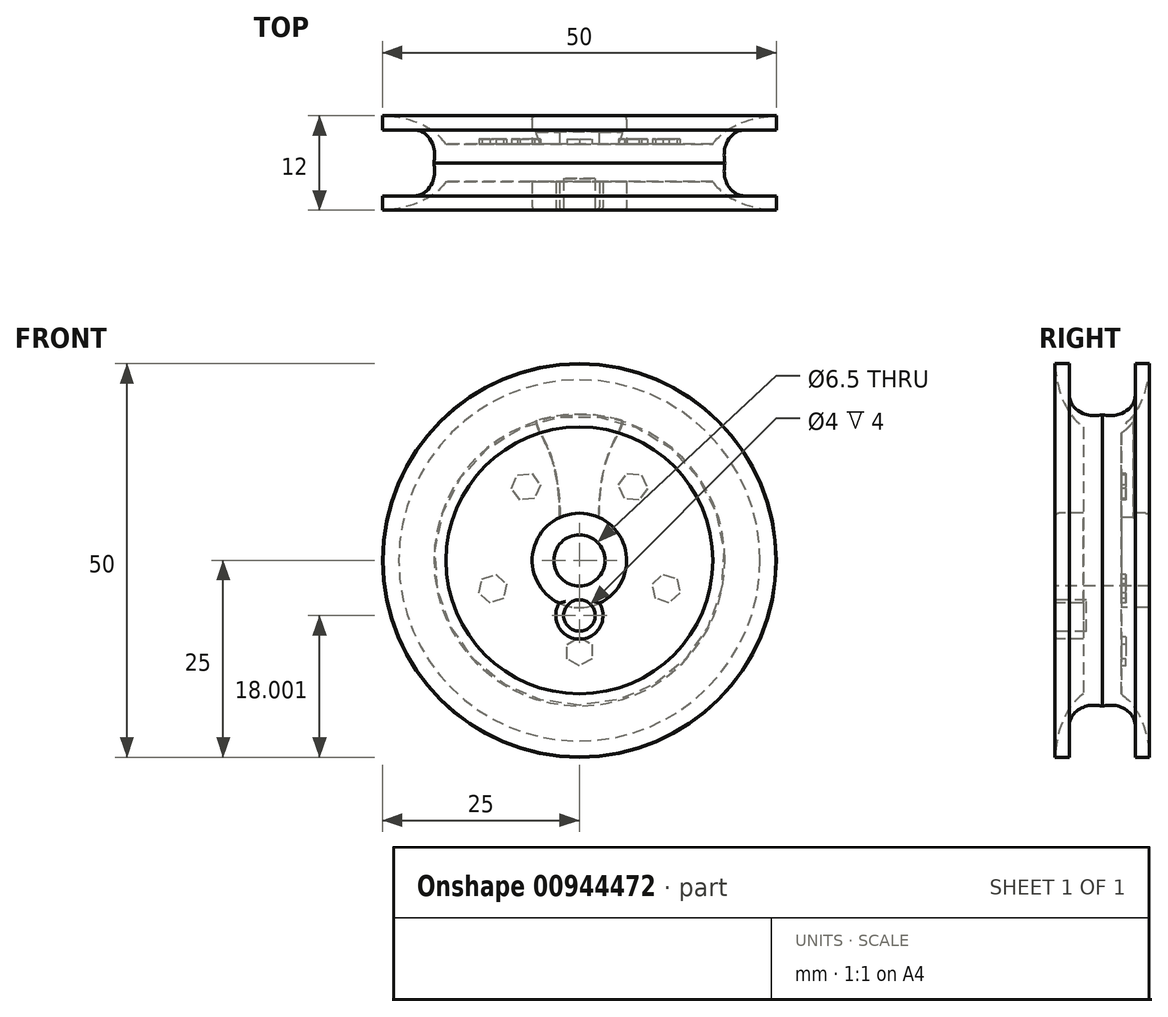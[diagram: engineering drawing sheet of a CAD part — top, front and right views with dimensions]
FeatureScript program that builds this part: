
annotation { "Feature Type Name" : "Feature", "Feature Type Description" : "" }
export const myFeature = defineFeature(function(context is Context, id is Id, definition is map)
    precondition{}
    {
        {
            var Q0;
            Q0=qCreatedBy(makeId("Front.planeOp"),FACE);
            var sketch = newSketch(context, id + "F0", { "sketchPlane" : qUnion([Q0])});
            skCircle(sketch, "E0", {"center": v(0, 0) * mm, "radius": 25 * mm});
            skSolve(sketch);
        }
        {
            var Q0;
            Q0 = qSketchRegion(id + "F0", true);
            extrude(context, id + "F1", {"entities" : qUnion([Q0]), "depth" : 12 * mm, "offsetDistance" : 25 * mm});
        }
        {
            var Q0;
            Q0=makeQuery(id+"F1.opExtrude","CAP_FACE",FACE,{"disambiguationData":[OSD([sQuery(id+"F0.wireOp",EDGE,"E0")])],"isStart":false});
            var sketch = newSketch(context, id + "F2", { "sketchPlane" : qUnion([Q0])});
            skSolve(sketch);
        }
        {
            var Q0;
            Q0=makeQuery(id+"F2.imprint","IMPRINT",FACE,{"disambiguationData":[TD([[makeQuery(id+"F2.imprint","IMPRINT",EDGE,{"derivedFrom":makeQuery(id+"F1.opExtrude","CAP_EDGE",EDGE,{"disambiguationData":[OSD([sQuery(id+"F0.wireOp",EDGE,"E0")])],"isStart":false})}),1.0]])]});
            var sketch = newSketch(context, id + "F3", { "sketchPlane" : qUnion([Q0])});
            skCircle(sketch, "E1", {"center": v(0, 0) * mm, "radius": 3.25 * mm});
            skSolve(sketch);
        }
        {
            var Q0;
            Q0 = qSketchRegion(id + "F3", true);
            extrude(context, id + "F4", {"entities" : qUnion([Q0]), "operationType" : NewBodyOperationType.REMOVE, "endBound" : BoundingType.THROUGH_ALL, "oppositeDirection" : true, "depth" : 25 * mm, "offsetDistance" : 25 * mm});
        }
        {
            var Q0;
            Q0=qCreatedBy(makeId("Top.planeOp"),FACE);
            var sketch = newSketch(context, id + "F5", { "sketchPlane" : qUnion([Q0])});
            skLineSegment(sketch, "E2", {"start": v(-24.95, 0) * mm, "end": v(-24.95, -3.6) * mm, "construction": true});
            skLineSegment(sketch, "E3", {"start": v(-24.95, -3.6) * mm, "end": v(-16.95, -3.6) * mm, "construction": true});
            skFitSpline(sketch, "E4", {"points": [v(-24.95, 0) * mm, v(-16.95, -3.6) * mm], "startDerivative": vector(8.9, -0.49) * mm, "endDerivative": vector(5.24, -7.32) * mm});
            skLineSegment(sketch, "E5", {"start": v(0, 0) * mm, "end": v(0, -6) * mm, "construction": true});
            skLineSegment(sketch, "E6", {"start": v(0, -6) * mm, "end": v(-25.37, -6) * mm, "construction": true});
            skLineSegment(sketch, "E7", {"start": v(0, 0) * mm, "end": v(-24.95, 0) * mm});
            skLineSegment(sketch, "E8", {"start": v(-16.95, -3.6) * mm, "end": v(0, -3.6) * mm});
            skLineSegment(sketch, "E9", {"start": v(0, -3.6) * mm, "end": v(0, 0) * mm});
            skLineSegment(sketch, "E10.MirrorCS", {"start": v(-16.95, -8.4) * mm, "end": v(0, -8.4) * mm});
            skFitSpline(sketch, "E11.MirrorCS", {"points": [v(-24.95, -12) * mm, v(-16.95, -8.4) * mm], "startDerivative": vector(8.9, 0.49) * mm, "endDerivative": vector(5.24, 7.32) * mm});
            skLineSegment(sketch, "E12.MirrorCS", {"start": v(0, -12) * mm, "end": v(-24.95, -12) * mm});
            skLineSegment(sketch, "E13.MirrorCS", {"start": v(0, -12) * mm, "end": v(0, -6) * mm, "construction": true});
            skLineSegment(sketch, "E14", {"start": v(0, -8.4) * mm, "end": v(0, -12) * mm});
            skLineSegment(sketch, "E15", {"start": v(-24.95, 0) * mm, "end": v(-24.95, -1.8) * mm, "construction": true});
            skLineSegment(sketch, "E16", {"start": v(-24.95, -1.8) * mm, "end": v(-22.95, -1.8) * mm, "construction": true});
            skLineSegment(sketch, "E17", {"start": v(-24.98, -6) * mm, "end": v(-18.48, -6) * mm});
            skFitSpline(sketch, "E18", {"points": [v(-22.95, -1.8) * mm, v(-18.48, -6) * mm], "startDerivative": vector(9.17, -0.94) * mm, "endDerivative": vector(0.05, -5.85) * mm});
            skLineSegment(sketch, "E19", {"start": v(-24.95, -1.8) * mm, "end": v(-26.85, -1.8) * mm});
            skLineSegment(sketch, "E20", {"start": v(-26.85, -1.8) * mm, "end": v(-25.37, -6) * mm});
            skLineSegment(sketch, "E21.MirrorCS", {"start": v(-26.85, -10.2) * mm, "end": v(-25.37, -6) * mm});
            skLineSegment(sketch, "E22.MirrorCS", {"start": v(-24.95, -10.2) * mm, "end": v(-26.85, -10.2) * mm});
            skLineSegment(sketch, "E23.MirrorCS", {"start": v(-24.95, -10.2) * mm, "end": v(-22.95, -10.2) * mm});
            skFitSpline(sketch, "E24.MirrorCS", {"points": [v(-22.95, -10.2) * mm, v(-18.48, -6) * mm], "startDerivative": vector(9.17, 0.94) * mm, "endDerivative": vector(0.05, 5.85) * mm});
            skLineSegment(sketch, "E25.MirrorCS", {"start": v(-24.95, -1.8) * mm, "end": v(-22.95, -1.8) * mm});
            skSolve(sketch);
        }
        {
            var Q0;
            Q0 = qSketchRegion(id + "F5", true);
            var Q1;
            Q1=sQuery(id+"F5.wireOp",EDGE,"E9");
            revolve(context, id + "F6", {"operationType" : NewBodyOperationType.REMOVE, "surfaceOperationType" : NewSurfaceOperationType.NEW, "entities" : qUnion([Q0]), "axis" : qUnion([Q1]), "revolveType" : RevolveType.FULL, "oppositeDirection" : true});
        }
        {
            var Q0;
            Q0=makeQuery(id+"F2.imprint","IMPRINT",FACE,{"disambiguationData":[TD([[makeQuery(id+"F2.imprint","IMPRINT",EDGE,{"derivedFrom":makeQuery(id+"F1.opExtrude","CAP_EDGE",EDGE,{"disambiguationData":[OSD([sQuery(id+"F0.wireOp",EDGE,"E0")])],"isStart":false})}),1.0]])]});
            var sketch = newSketch(context, id + "F7", { "sketchPlane" : qUnion([Q0])});
            skCircle(sketch, "E26", {"center": v(0, 0) * mm, "radius": 6 * mm});
            skCircle(sketch, "E27.0", {"center": v(0, 0) * mm, "radius": 3.25 * mm});
            skSolve(sketch);
        }
        {
            var Q0;
            Q0 = qSketchRegion(id + "F7", true);
            extrude(context, id + "F8", {"entities" : qUnion([Q0]), "operationType" : NewBodyOperationType.ADD, "oppositeDirection" : true, "depth" : 12 * mm, "offsetDistance" : 25 * mm});
        }
        {
            var Q0;
            Q0=qCreatedBy(makeId("Front.planeOp"),FACE);
            cPlane(context, id + "F9", {"entities" : qUnion([Q0]), "cplaneType" : CPlaneType.OFFSET, "offset" : 4 * mm, "width" : 150 * mm, "height" : 150 * mm});
        }
        {
            var Q0;
            Q0=qCreatedBy(id+"F9.planeOp",FACE);
            var sketch = newSketch(context, id + "F10", { "sketchPlane" : qUnion([Q0])});
            skLineSegment(sketch, "E28", {"start": v(0, 0) * mm, "end": v(0, 21.23) * mm, "construction": true});
            skLineSegment(sketch, "E29", {"start": v(0, 5.32) * mm, "end": v(-2.5, 5.32) * mm});
            skLineSegment(sketch, "E30", {"start": v(0, 16.33) * mm, "end": v(-4.5, 16.33) * mm, "construction": true});
            skFitSpline(sketch, "E31", {"points": [v(-2.5, 5.32) * mm, v(-5.5, 17.52) * mm, v(-5.5, 18.88) * mm], "startDerivative": vector(-0.22, 33.82) * mm, "endDerivative": vector(0.1, 0.5) * mm});
            skLineSegment(sketch, "E32", {"start": v(-5.5, 18.88) * mm, "end": v(0, 18.88) * mm});
            skLineSegment(sketch, "E33.MirrorCS", {"start": v(5.5, 18.88) * mm, "end": v(0, 18.88) * mm});
            skFitSpline(sketch, "E34.MirrorCS", {"points": [v(2.5, 5.32) * mm, v(5.5, 17.52) * mm, v(5.5, 18.88) * mm], "startDerivative": vector(0.22, 33.82) * mm, "endDerivative": vector(-0.1, 0.5) * mm});
            skLineSegment(sketch, "E35.MirrorCS", {"start": v(0, 5.32) * mm, "end": v(2.5, 5.32) * mm});
            skSolve(sketch);
        }
        {
            var Q0;
            Q0=qCreatedBy(makeId("Top.planeOp"),FACE);
            var sketch = newSketch(context, id + "F11", { "sketchPlane" : qUnion([Q0])});
            skLineSegment(sketch, "E36", {"start": v(0, 0) * mm, "end": v(0, 18.3) * mm, "construction": true});
            skSolve(sketch);
        }
        {
            var Q0;
            Q0 = qSketchRegion(id + "F10", true);
            extrude(context, id + "F12", {"entities" : qUnion([Q0]), "operationType" : NewBodyOperationType.ADD, "oppositeDirection" : true, "depth" : 2 * mm, "offsetDistance" : 25 * mm});
        }
        {
            var Q0;
            Q0=qCreatedBy(makeId("Top.planeOp"),FACE);
            var sketch = newSketch(context, id + "F13", { "sketchPlane" : qUnion([Q0])});
            skLineSegment(sketch, "E37.0", {"start": v(25, -1.8) * mm, "end": v(22.95, -1.8) * mm});
            skFitSpline(sketch, "E38", {"points": [v(-22.95, -1.8) * mm, v(-19.9, -2.11) * mm, v(-18.5, -4.05) * mm, v(-18.48, -6) * mm]});
            skFitSpline(sketch, "E39", {"points": [v(18.48, -6) * mm, v(18.5, -4.05) * mm, v(19.9, -2.11) * mm, v(22.95, -1.8) * mm]});
            skFitSpline(sketch, "E40", {"points": [v(-22.95, -10.2) * mm, v(-19.9, -9.89) * mm, v(-18.5, -7.95) * mm, v(-18.48, -6) * mm]});
            skFitSpline(sketch, "E41", {"points": [v(18.48, -6) * mm, v(18.5, -7.95) * mm, v(19.9, -9.89) * mm, v(22.95, -10.2) * mm]});
            skLineSegment(sketch, "E42.trimOffspring", {"start": v(-22.95, -1.8) * mm, "end": v(-25, -1.8) * mm});
            skLineSegment(sketch, "E43", {"start": v(-22.95, -10.2) * mm, "end": v(-27.99, -10.2) * mm});
            skLineSegment(sketch, "E44", {"start": v(-27.99, -10.2) * mm, "end": v(-25, -1.8) * mm});
            skLineSegment(sketch, "E45", {"start": v(0, 0) * mm, "end": v(0, -9.4) * mm});
            skSolve(sketch);
        }
        {
            var Q0;
            Q0 = qSketchRegion(id + "F13", true);
            var Q1;
            Q1=sQuery(id+"F13.wireOp",EDGE,"E45");
            revolve(context, id + "F14", {"operationType" : NewBodyOperationType.REMOVE, "surfaceOperationType" : NewSurfaceOperationType.NEW, "entities" : qUnion([Q0]), "axis" : qUnion([Q1]), "revolveType" : RevolveType.FULL, "oppositeDirection" : true});
        }
        {
            var Q0;
            Q0=qCreatedBy(id+"F9.planeOp",FACE);
            var sketch = newSketch(context, id + "F15", { "sketchPlane" : qUnion([Q0])});
            skLineSegment(sketch, "E46", {"start": v(0, -5.64) * mm, "end": v(0, -9.64) * mm, "construction": true});
            skPoint(sketch, "E47", {"position": v(0, -11.57) * mm});
            skCircle(sketch, "E48.cCircle", {"center": v(0, -11.57) * mm, "radius": 1.6 * mm, "construction": true});
            skLineSegment(sketch, "E48.0", {"start": v(1.6, -10.65) * mm, "end": v(1.6, -12.5) * mm});
            skLineSegment(sketch, "E48.1", {"start": v(1.6, -12.5) * mm, "end": v(0, -13.41) * mm});
            skLineSegment(sketch, "E48.2", {"start": v(0, -13.41) * mm, "end": v(-1.6, -12.5) * mm});
            skLineSegment(sketch, "E48.3", {"start": v(-1.6, -12.5) * mm, "end": v(-1.6, -10.65) * mm});
            skLineSegment(sketch, "E48.4", {"start": v(-1.6, -10.65) * mm, "end": v(0, -9.73) * mm});
            skLineSegment(sketch, "E48.5", {"start": v(0, -9.73) * mm, "end": v(1.6, -10.65) * mm});
            skPoint(sketch, "E48.0.midPoint", {"position": v(1.6, -11.57) * mm});
            skLineSegment(sketch, "E49.1.0", {"start": v(12.37, -2.34) * mm, "end": v(12.76, -4.14) * mm});
            skLineSegment(sketch, "E49.1.1", {"start": v(12.76, -4.14) * mm, "end": v(11.39, -5.38) * mm});
            skLineSegment(sketch, "E49.1.2", {"start": v(11.39, -5.38) * mm, "end": v(9.64, -4.8) * mm});
            skLineSegment(sketch, "E49.1.3", {"start": v(9.64, -4.8) * mm, "end": v(9.25, -3) * mm});
            skLineSegment(sketch, "E49.1.4", {"start": v(9.25, -3) * mm, "end": v(10.62, -1.78) * mm});
            skLineSegment(sketch, "E49.1.5", {"start": v(10.62, -1.78) * mm, "end": v(12.37, -2.34) * mm});
            skLineSegment(sketch, "E49.2.0", {"start": v(6.05, 11.04) * mm, "end": v(7.88, 10.85) * mm});
            skLineSegment(sketch, "E49.2.1", {"start": v(7.88, 10.85) * mm, "end": v(8.63, 9.17) * mm});
            skLineSegment(sketch, "E49.2.2", {"start": v(8.63, 9.17) * mm, "end": v(7.55, 7.68) * mm});
            skLineSegment(sketch, "E49.2.3", {"start": v(7.55, 7.68) * mm, "end": v(5.72, 7.87) * mm});
            skLineSegment(sketch, "E49.2.4", {"start": v(5.72, 7.87) * mm, "end": v(4.97, 9.55) * mm});
            skLineSegment(sketch, "E49.2.5", {"start": v(4.97, 9.55) * mm, "end": v(6.05, 11.04) * mm});
            skLineSegment(sketch, "E49.3.0", {"start": v(-8.63, 9.17) * mm, "end": v(-7.88, 10.85) * mm});
            skLineSegment(sketch, "E49.3.1", {"start": v(-7.88, 10.85) * mm, "end": v(-6.05, 11.04) * mm});
            skLineSegment(sketch, "E49.3.2", {"start": v(-6.05, 11.04) * mm, "end": v(-4.97, 9.55) * mm});
            skLineSegment(sketch, "E49.3.3", {"start": v(-4.97, 9.55) * mm, "end": v(-5.72, 7.87) * mm});
            skLineSegment(sketch, "E49.3.4", {"start": v(-5.72, 7.87) * mm, "end": v(-7.55, 7.68) * mm});
            skLineSegment(sketch, "E49.3.5", {"start": v(-7.55, 7.68) * mm, "end": v(-8.63, 9.17) * mm});
            skLineSegment(sketch, "E49.4.0", {"start": v(-11.39, -5.38) * mm, "end": v(-12.76, -4.14) * mm});
            skLineSegment(sketch, "E49.4.1", {"start": v(-12.76, -4.14) * mm, "end": v(-12.37, -2.34) * mm});
            skLineSegment(sketch, "E49.4.2", {"start": v(-12.37, -2.34) * mm, "end": v(-10.62, -1.78) * mm});
            skLineSegment(sketch, "E49.4.3", {"start": v(-10.62, -1.78) * mm, "end": v(-9.25, -3) * mm});
            skLineSegment(sketch, "E49.4.4", {"start": v(-9.25, -3) * mm, "end": v(-9.64, -4.8) * mm});
            skLineSegment(sketch, "E49.4.5", {"start": v(-9.64, -4.8) * mm, "end": v(-11.39, -5.38) * mm});
            skPoint(sketch, "E49.center", {"position": v(0, 0) * mm});
            skSolve(sketch);
        }
        {
            var Q0;
            Q0 = qSketchRegion(id + "F15", true);
            extrude(context, id + "F16", {"entities" : qUnion([Q0]), "operationType" : NewBodyOperationType.ADD, "oppositeDirection" : true, "depth" : 1 * mm, "offsetDistance" : 25 * mm});
        }
        {
            var Q0;
            Q0=makeQuery(id+"F2.imprint","IMPRINT",FACE,{"disambiguationData":[TD([[makeQuery(id+"F2.imprint","IMPRINT",EDGE,{"derivedFrom":makeQuery(id+"F1.opExtrude","CAP_EDGE",EDGE,{"disambiguationData":[OSD([sQuery(id+"F0.wireOp",EDGE,"E0")])],"isStart":false})}),1.0]])]});
            var sketch = newSketch(context, id + "F17", { "sketchPlane" : qUnion([Q0])});
            skLineSegment(sketch, "E50", {"start": v(0, -25) * mm, "end": v(0, -5) * mm, "construction": true});
            skLineSegment(sketch, "E51", {"start": v(0, -5) * mm, "end": v(0, -7) * mm, "construction": true});
            skCircle(sketch, "E52", {"center": v(0, -7) * mm, "radius": 2 * mm});
            skCircle(sketch, "E53", {"center": v(0, -7) * mm, "radius": 3 * mm});
            skSolve(sketch);
        }
        {
            var Q0;
            Q0=makeQuery(id+"F17.imprint","IMPRINT",FACE,{"disambiguationData":[TD([[makeQuery(id+"F17.imprint","IMPRINT",EDGE,{"derivedFrom":sQuery(id+"F17.wireOp",EDGE,"E52")}),-1.0]])]});
            var Q1;
            Q1=sQuery(id+"F17.wireOp",EDGE,"E53");
            var Q2;
            Q2=sQuery(id+"F17.wireOp",EDGE,"E52");
            extrude(context, id + "F18", {"entities" : qUnion([Q0]), "operationType" : NewBodyOperationType.ADD, "surfaceEntities" : qUnion([Q1, Q2]), "oppositeDirection" : true, "depth" : 4 * mm, "offsetDistance" : 25 * mm});
        }
        {
            var Q0;
            Q0=makeQuery(id+"F2.imprint","IMPRINT",FACE,{"disambiguationData":[TD([[makeQuery(id+"F2.imprint","IMPRINT",EDGE,{"derivedFrom":makeQuery(id+"F1.opExtrude","CAP_EDGE",EDGE,{"disambiguationData":[OSD([sQuery(id+"F0.wireOp",EDGE,"E0")])],"isStart":false})}),1.0]])]});
            var sketch = newSketch(context, id + "F19", { "sketchPlane" : qUnion([Q0])});
            skArc(sketch, "E54.0", {"start": v(-1.6, -5.79) * mm, "mid": v(0, -9) * mm, "end": v(1.6, -5.79) * mm});
            skCircle(sketch, "E55", {"center": v(0, -7) * mm, "radius": 2 * mm});
            skSolve(sketch);
        }
        {
            var Q0;
            Q0 = qSketchRegion(id + "F19", true);
            extrude(context, id + "F20", {"entities" : qUnion([Q0]), "operationType" : NewBodyOperationType.REMOVE, "oppositeDirection" : true, "depth" : 4 * mm, "offsetDistance" : 25 * mm});
        }
        {
            var Q0;
            Q0=makeQuery(id+"F18.opExtrude","CAP_EDGE",EDGE,{"disambiguationData":[OSD([sQuery(id+"F17.wireOp",EDGE,"E53")])],"isStart":true});
            var Q1;
            Q1=makeQuery(id+"F20.boolean.opBoolean","MERGE",EDGE,{"derivedFrom":[makeQuery(id+"F18.opExtrude","CAP_EDGE",EDGE,{"disambiguationData":[OSD([sQuery(id+"F17.wireOp",EDGE,"E52")])],"isStart":true})],"fromTools":[makeQuery(id+"F20.opExtrude","CAP_EDGE",EDGE,{"disambiguationData":[OSD([sQuery(id+"F19.wireOp",EDGE,"E55")])],"isStart":true})]});
            var Q2;
            {var subQ0=sQuery(id+"F7.wireOp",EDGE,"E26");var subQ1=sQuery(id+"F17.wireOp",EDGE,"E53");Q2=makeQuery(id+"F18.boolean.opBoolean","SPLIT",EDGE,{"disambiguationData":[TD([makeQuery(id+"F18.opExtrude","SWEPT_FACE",FACE,{"disambiguationData":[OSD([subQ1])]})])],"derivedFrom":makeQuery(id+"F8.opExtrude","CAP_EDGE",EDGE,{"disambiguationData":[OSD([subQ0])],"isStart":true})});}
            var Q3;
            Q3=makeQuery(id+"F8.opExtrude","CAP_EDGE",EDGE,{"disambiguationData":[OSD([sQuery(id+"F7.wireOp",EDGE,"E26")])],"isStart":false});
            fillet(context, id + "F21", {"entities" : qUnion([Q0, Q1, Q2, Q3]), "radius" : 0.5 * mm, "tangentPropagation" : true, "allowEdgeOverflow" : false});
        }
        {
            var Q0;
            Q0=makeQuery(id+"F2PfkVp5y3bRrNf_1.1.F12.opExtrude","CAP_EDGE",EDGE,{"disambiguationData":[OSD([sQuery(id+"F10.wireOp",EDGE,"E34.MirrorCS")])],"isStart":false});
            var Q1;
            Q1=makeQuery(id+"F2PfkVp5y3bRrNf_1.1.F12.opExtrude","CAP_EDGE",EDGE,{"disambiguationData":[OSD([sQuery(id+"F10.wireOp",EDGE,"E31")])],"isStart":false});
            var Q2;
            Q2=makeQuery(id+"F12.opExtrude","CAP_EDGE",EDGE,{"disambiguationData":[OSD([sQuery(id+"F10.wireOp",EDGE,"E34.MirrorCS")])],"isStart":false});
            var Q3;
            Q3=makeQuery(id+"F12.opExtrude","CAP_EDGE",EDGE,{"disambiguationData":[OSD([sQuery(id+"F10.wireOp",EDGE,"E31")])],"isStart":false});
            var Q4;
            Q4=makeQuery(id+"F2PfkVp5y3bRrNf_1.4.F12.opExtrude","CAP_EDGE",EDGE,{"disambiguationData":[OSD([sQuery(id+"F10.wireOp",EDGE,"E34.MirrorCS")])],"isStart":false});
            var Q5;
            Q5=makeQuery(id+"F2PfkVp5y3bRrNf_1.4.F12.opExtrude","CAP_EDGE",EDGE,{"disambiguationData":[OSD([sQuery(id+"F10.wireOp",EDGE,"E31")])],"isStart":false});
            var Q6;
            Q6=makeQuery(id+"F2PfkVp5y3bRrNf_1.2.F12.opExtrude","CAP_EDGE",EDGE,{"disambiguationData":[OSD([sQuery(id+"F10.wireOp",EDGE,"E31")])],"isStart":false});
            var Q7;
            Q7=makeQuery(id+"F2PfkVp5y3bRrNf_1.2.F12.opExtrude","CAP_EDGE",EDGE,{"disambiguationData":[OSD([sQuery(id+"F10.wireOp",EDGE,"E34.MirrorCS")])],"isStart":false});
            var Q8;
            Q8=makeQuery(id+"F2PfkVp5y3bRrNf_1.3.F12.opExtrude","CAP_EDGE",EDGE,{"disambiguationData":[OSD([sQuery(id+"F10.wireOp",EDGE,"E31")])],"isStart":false});
            fillet(context, id + "F22", {"entities" : qUnion([Q0, Q1, Q2, Q3, Q4, Q5, Q6, Q7, Q8]), "radius" : 0.1 * mm, "tangentPropagation" : true, "allowEdgeOverflow" : false});
        }
    });
